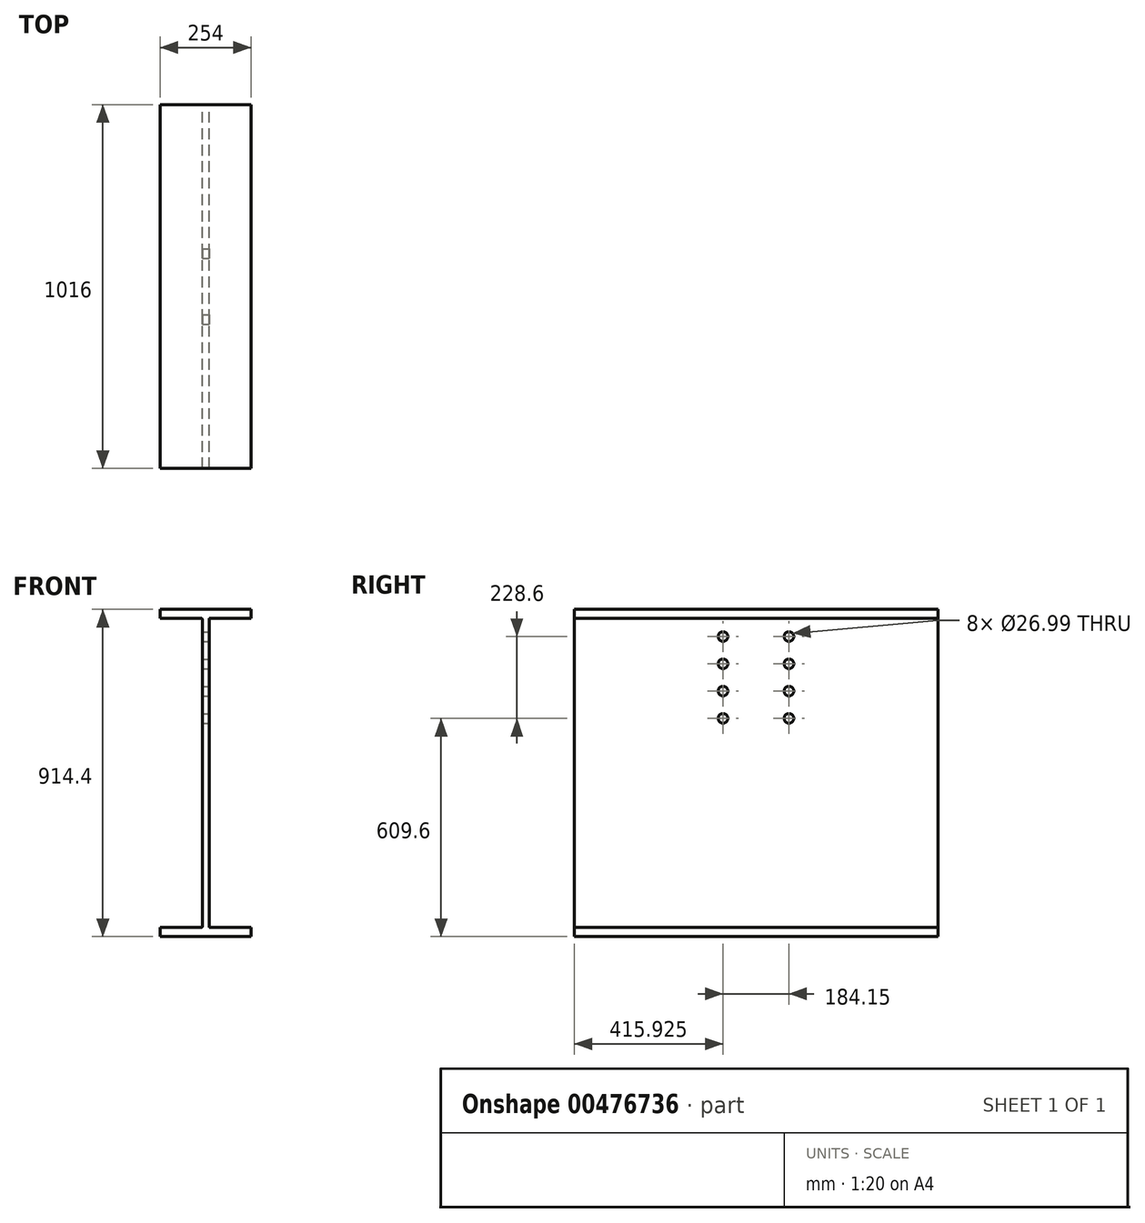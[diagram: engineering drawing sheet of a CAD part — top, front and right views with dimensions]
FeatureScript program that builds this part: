
annotation { "Feature Type Name" : "Feature", "Feature Type Description" : "" }
export const myFeature = defineFeature(function(context is Context, id is Id, definition is map)
    precondition{}
    {
        {
            var Q0;
            Q0=qCreatedBy(makeId("Front.planeOp"),FACE);
            var sketch = newSketch(context, id + "F0", { "sketchPlane" : qUnion([Q0])});
            skLineSegment(sketch, "E0", {"start": v(127, -431.8) * mm, "end": v(12.06, -431.8) * mm});
            skLineSegment(sketch, "E1", {"start": v(9.52, -429.26) * mm, "end": v(9.52, 429.26) * mm});
            skLineSegment(sketch, "E2", {"start": v(12.07, 431.8) * mm, "end": v(127, 431.8) * mm});
            skLineSegment(sketch, "E3", {"start": v(-127, 431.8) * mm, "end": v(-12.06, 431.8) * mm});
            skLineSegment(sketch, "E4", {"start": v(-9.53, 429.26) * mm, "end": v(-9.53, -429.26) * mm});
            skLineSegment(sketch, "E5", {"start": v(-12.06, -431.8) * mm, "end": v(-127, -431.8) * mm});
            skLineSegment(sketch, "E6", {"start": v(0, 0) * mm, "end": v(-9.52, 0) * mm, "construction": true});
            skLineSegment(sketch, "E7", {"start": v(0, 0) * mm, "end": v(9.52, 0) * mm, "construction": true});
            skLineSegment(sketch, "E8", {"start": v(0, 0) * mm, "end": v(0, 457.2) * mm, "construction": true});
            skLineSegment(sketch, "E9", {"start": v(0, 0) * mm, "end": v(0, -457.2) * mm, "construction": true});
            skPoint(sketch, "E10.visualSharp", {"position": v(-9.53, 431.8) * mm});
            skArc(sketch, "E10.filletArc", {"start": v(-9.52, 429.26) * mm, "mid": v(-10.27, 431.06) * mm, "end": v(-12.06, 431.8) * mm});
            skPoint(sketch, "E11.visualSharp", {"position": v(9.53, 431.8) * mm});
            skArc(sketch, "E11.filletArc", {"start": v(12.07, 431.8) * mm, "mid": v(10.27, 431.06) * mm, "end": v(9.52, 429.26) * mm});
            skPoint(sketch, "E12.visualSharp", {"position": v(9.53, -431.8) * mm});
            skArc(sketch, "E12.filletArc", {"start": v(9.52, -429.26) * mm, "mid": v(10.27, -431.06) * mm, "end": v(12.06, -431.8) * mm});
            skPoint(sketch, "E13.visualSharp", {"position": v(-9.53, -431.8) * mm});
            skArc(sketch, "E13.filletArc", {"start": v(-12.06, -431.8) * mm, "mid": v(-10.27, -431.06) * mm, "end": v(-9.52, -429.26) * mm});
            skPoint(sketch, "E14.visualSharp", {"position": v(-127, 457.2) * mm});
            skPoint(sketch, "E15.visualSharp", {"position": v(127, 457.2) * mm});
            skPoint(sketch, "E16.visualSharp", {"position": v(127, 431.8) * mm});
            skPoint(sketch, "E17.visualSharp", {"position": v(127, -457.2) * mm});
            skPoint(sketch, "E18.visualSharp", {"position": v(-127, -431.8) * mm});
            skPoint(sketch, "E19.visualSharp", {"position": v(-127, -457.2) * mm});
            skLineSegment(sketch, "E20", {"start": v(127, -431.8) * mm, "end": v(127, -457.2) * mm});
            skLineSegment(sketch, "E21", {"start": v(-127, -431.8) * mm, "end": v(-127, -457.2) * mm});
            skLineSegment(sketch, "E22", {"start": v(-127, 457.2) * mm, "end": v(-127, 431.8) * mm});
            skLineSegment(sketch, "E23", {"start": v(127, 457.2) * mm, "end": v(127, 431.8) * mm});
            skLineSegment(sketch, "E24", {"start": v(-127, 457.2) * mm, "end": v(127, 457.2) * mm});
            skLineSegment(sketch, "E25", {"start": v(-127, -457.2) * mm, "end": v(127, -457.2) * mm});
            skSolve(sketch);
        }
        {
            var Q0;
            Q0=makeQuery(id+"F0.imprint","IMPRINT",FACE,{"disambiguationData":[TD([[makeQuery(id+"F0.imprint","IMPRINT",EDGE,{"derivedFrom":sQuery(id+"F0.wireOp",EDGE,"E0")}),1.0]])]});
            extrude(context, id + "F1", {"entities" : qUnion([Q0]), "endBound" : BoundingType.SYMMETRIC, "depth" : 1016 * mm});
        }
        {
            var Q0;
            Q0=makeQuery(id+"F1.opExtrude","SWEPT_FACE",FACE,{"disambiguationData":[OSD([sQuery(id+"F0.wireOp",EDGE,"E1")])]});
            var sketch = newSketch(context, id + "F2", { "sketchPlane" : qUnion([Q0])});
            skPoint(sketch, "E26", {"position": v(92.08, 381) * mm});
            skPoint(sketch, "E27", {"position": v(92.08, 304.8) * mm});
            skPoint(sketch, "E28", {"position": v(92.08, 228.6) * mm});
            skPoint(sketch, "E29", {"position": v(92.08, 152.4) * mm});
            skLineSegment(sketch, "E30", {"start": v(0, 485.51) * mm, "end": v(0, -127.3) * mm, "construction": true});
            skPoint(sketch, "E31.MirrorP", {"position": v(-92.08, 381) * mm});
            skPoint(sketch, "E32.MirrorP", {"position": v(-92.07, 304.8) * mm});
            skPoint(sketch, "E33.MirrorP", {"position": v(-92.07, 228.6) * mm});
            skPoint(sketch, "E34.MirrorP", {"position": v(-92.08, 152.4) * mm});
            skSolve(sketch);
        }
        {
            var Q0;
            Q0=sQuery(id+"F2.wireOp",VERTEX,"E26");
            var Q1;
            Q1=sQuery(id+"F2.wireOp",VERTEX,"E27");
            var Q2;
            Q2=sQuery(id+"F2.wireOp",VERTEX,"E28");
            var Q3;
            Q3=sQuery(id+"F2.wireOp",VERTEX,"E29");
            var Q4;
            Q4=makeQuery(id+"F1.opExtrude","SWEPT_BODY",BODY,{"disambiguationData":[OSD([sQuery(id+"F0.wireOp",EDGE,"E0"),sQuery(id+"F0.wireOp",EDGE,"E1"),sQuery(id+"F0.wireOp",EDGE,"E2"),sQuery(id+"F0.wireOp",EDGE,"E3"),sQuery(id+"F0.wireOp",EDGE,"E4"),sQuery(id+"F0.wireOp",EDGE,"E5"),sQuery(id+"F0.wireOp",EDGE,"E10.filletArc"),sQuery(id+"F0.wireOp",EDGE,"E11.filletArc"),sQuery(id+"F0.wireOp",EDGE,"E12.filletArc"),sQuery(id+"F0.wireOp",EDGE,"E13.filletArc"),sQuery(id+"F0.wireOp",EDGE,"E20"),sQuery(id+"F0.wireOp",EDGE,"E21"),sQuery(id+"F0.wireOp",EDGE,"E22"),sQuery(id+"F0.wireOp",EDGE,"E23"),sQuery(id+"F0.wireOp",EDGE,"E24"),sQuery(id+"F0.wireOp",EDGE,"E25")])]});
            hole(context, id + "F3", {"style" : HoleStyle.SIMPLE, "endStyle" : HoleEndStyle.BLIND, "holeDiameter" : 26.99 * mm, "holeDepth" : 25.4 * mm, "isTappedThrough" : true, "tappedDepth" : 12.7 * mm, "tapClearance" : 3, "locations" : qUnion([Q0, Q1, Q2, Q3]), "scope" : qUnion([Q4])});
        }
        {
            var Q0;
            Q0=sQuery(id+"F2.wireOp",VERTEX,"E31.MirrorP");
            var Q1;
            Q1=sQuery(id+"F2.wireOp",VERTEX,"E32.MirrorP");
            var Q2;
            Q2=sQuery(id+"F2.wireOp",VERTEX,"E33.MirrorP");
            var Q3;
            Q3=sQuery(id+"F2.wireOp",VERTEX,"E34.MirrorP");
            var Q4;
            Q4=makeQuery(id+"F1.opExtrude","SWEPT_BODY",BODY,{"disambiguationData":[OSD([sQuery(id+"F0.wireOp",EDGE,"E0"),sQuery(id+"F0.wireOp",EDGE,"E1"),sQuery(id+"F0.wireOp",EDGE,"E2"),sQuery(id+"F0.wireOp",EDGE,"E3"),sQuery(id+"F0.wireOp",EDGE,"E4"),sQuery(id+"F0.wireOp",EDGE,"E5"),sQuery(id+"F0.wireOp",EDGE,"E10.filletArc"),sQuery(id+"F0.wireOp",EDGE,"E11.filletArc"),sQuery(id+"F0.wireOp",EDGE,"E12.filletArc"),sQuery(id+"F0.wireOp",EDGE,"E13.filletArc"),sQuery(id+"F0.wireOp",EDGE,"E20"),sQuery(id+"F0.wireOp",EDGE,"E21"),sQuery(id+"F0.wireOp",EDGE,"E22"),sQuery(id+"F0.wireOp",EDGE,"E23"),sQuery(id+"F0.wireOp",EDGE,"E24"),sQuery(id+"F0.wireOp",EDGE,"E25")])]});
            hole(context, id + "F4", {"style" : HoleStyle.SIMPLE, "endStyle" : HoleEndStyle.BLIND, "holeDiameter" : 26.99 * mm, "holeDepth" : 25.4 * mm, "isTappedThrough" : true, "tappedDepth" : 12.7 * mm, "tapClearance" : 3, "locations" : qUnion([Q0, Q1, Q2, Q3]), "scope" : qUnion([Q4])});
        }
    });
